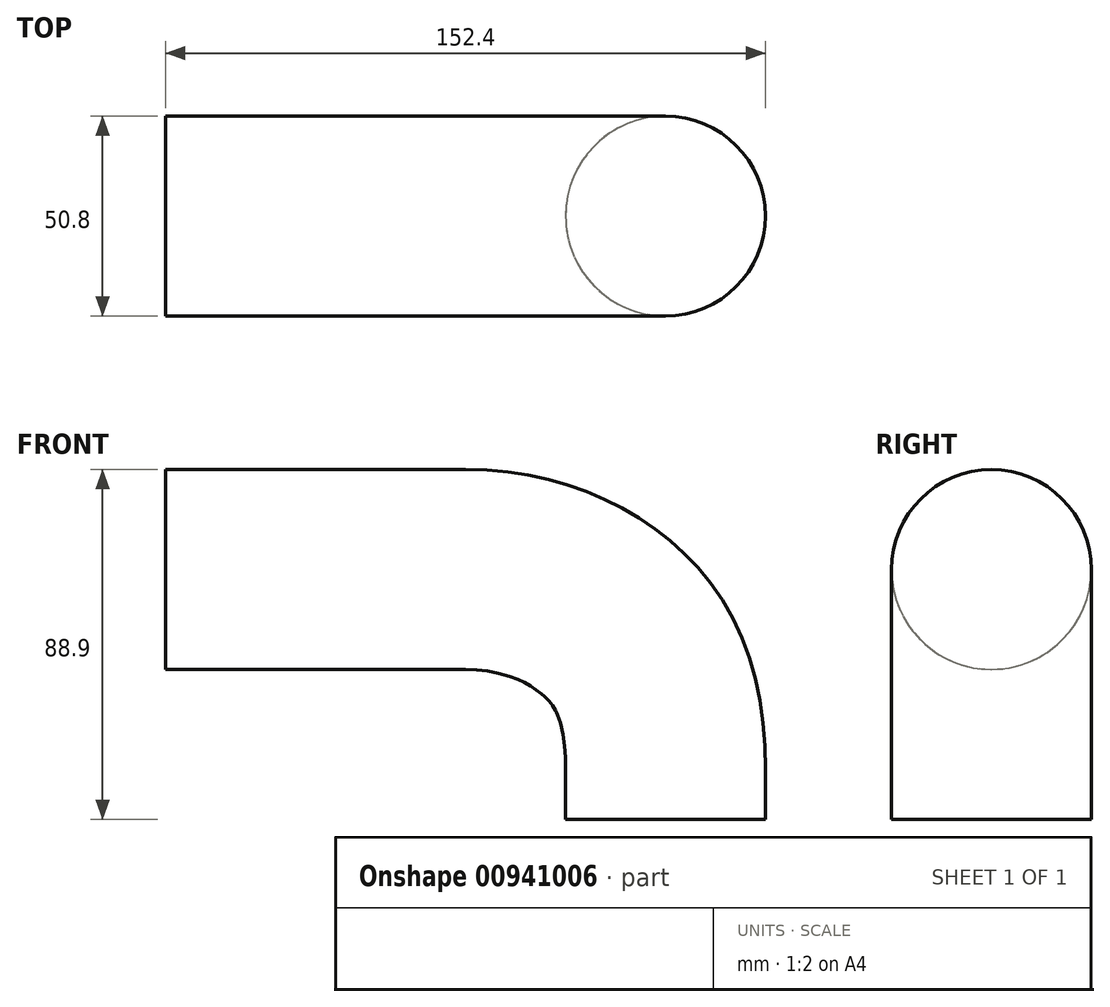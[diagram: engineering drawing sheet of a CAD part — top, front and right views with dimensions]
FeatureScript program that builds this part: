
annotation { "Feature Type Name" : "Feature", "Feature Type Description" : "" }
export const myFeature = defineFeature(function(context is Context, id is Id, definition is map)
    precondition{}
    {
        {
            var Q0;
            Q0=qCreatedBy(makeId("Front.planeOp"),FACE);
            var sketch = newSketch(context, id + "F0", { "sketchPlane" : qUnion([Q0])});
            skFitSpline(sketch, "E0", {"points": [v(-50.8, 50.8) * mm, v(-14.32, 37.92) * mm, v(0, 0) * mm], "startDerivative": vector(90.92, 0) * mm, "endDerivative": vector(0, -112.85) * mm});
            skSolve(sketch);
        }
        {
            var Q0;
            Q0=qCreatedBy(makeId("Top.planeOp"),FACE);
            var sketch = newSketch(context, id + "F1", { "sketchPlane" : qUnion([Q0])});
            skCircle(sketch, "E1", {"center": v(0, 0) * mm, "radius": 25.4 * mm});
            skSolve(sketch);
        }
        {
            var Q0;
            Q0=makeQuery(id+"F1.imprint","IMPRINT",FACE,{"disambiguationData":[TD([[makeQuery(id+"F1.imprint","IMPRINT",EDGE,{"derivedFrom":sQuery(id+"F1.wireOp",EDGE,"E1")}),1.0]])]});
            var Q1;
            Q1=sQuery(id+"F0.wireOp",EDGE,"E0");
            sweep(context, id + "F2", {"profiles" : qUnion([Q0]), "path" : qUnion([Q1])});
        }
        {
            var Q0;
            Q0=makeQuery(id+"F2.opSweep","CAP_FACE",FACE,{"disambiguationData":[OSD([sQuery(id+"F0.wireOp",VERTEX,"E0.end"),sQuery(id+"F1.wireOp",EDGE,"E1")])],"isStart":true});
            extrude(context, id + "F3", {"entities" : qUnion([Q0]), "operationType" : NewBodyOperationType.ADD, "depth" : 12.7 * mm, "offsetDistance" : 25.4 * mm});
        }
        {
            var Q0;
            Q0=makeQuery(id+"F2.opSweep","CAP_FACE",FACE,{"disambiguationData":[OSD([sQuery(id+"F0.wireOp",VERTEX,"E0.start"),sQuery(id+"F1.wireOp",EDGE,"E1")])],"isStart":false});
            extrude(context, id + "F4", {"entities" : qUnion([Q0]), "operationType" : NewBodyOperationType.ADD, "depth" : 76.2 * mm, "offsetDistance" : 25.4 * mm});
        }
    });
